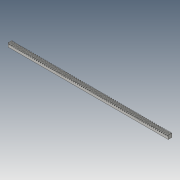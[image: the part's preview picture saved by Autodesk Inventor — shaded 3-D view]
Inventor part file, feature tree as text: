
AUTODESK INVENTOR PART (.ipt)
format: ipt  version: 2016 (Build 200138000, 138)  size: 1,425,920 bytes
history: native  units: in
note: dims shown in document units (in); Inventor stores cm internally (conversion verified against a paired STEP export)
features: other x2, extrude x1, sketch x1
ambient origin geometry x8: Origin, YZ Plane, XZ Plane, XY Plane, X Axis, Y Axis, Z Axis, Center Point
bodies: Solid1 (feature_tree)
feature tree (4):
  other  "6295K110_MTL GEAR RACK--14-.5 DEG PRESSURE ANGLE.SLDPRT"
  extrude  "Extrusion1"  [1 undecoded]
  sketch  "Sketch1"  dims[d0=1.0in d1=0.0in]
  other  "LPattern4"
note: 1 required parameter value undecoded (feature->parameter linkage not recoverable at this tier; creation-order binding heuristic only, values carry confidence <= 0.55)
